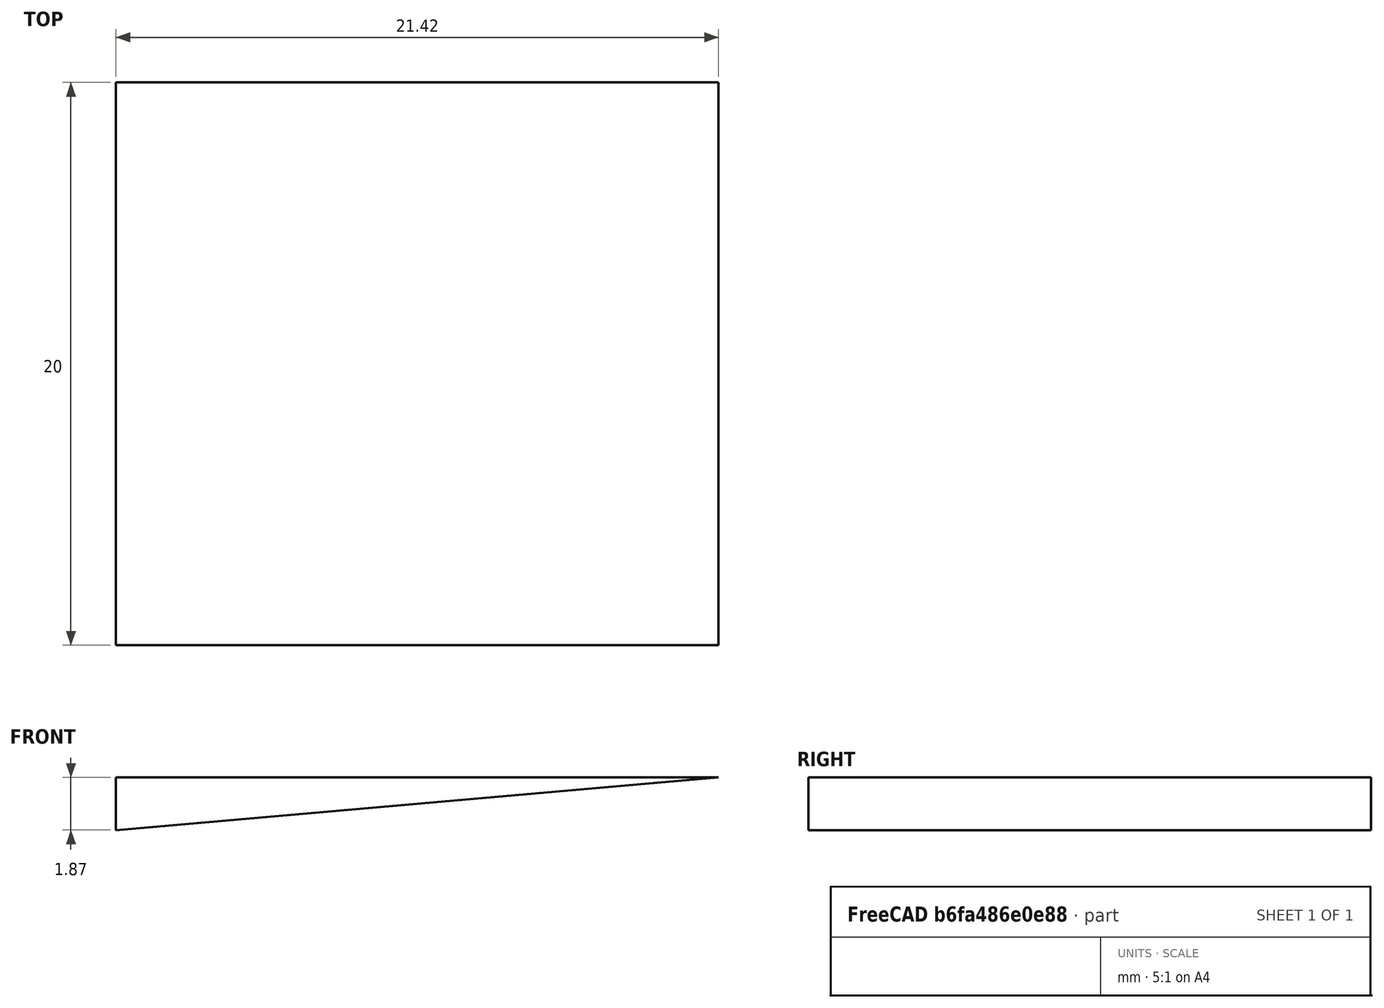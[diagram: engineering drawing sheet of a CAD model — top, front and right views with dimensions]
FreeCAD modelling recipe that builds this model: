
FCSTD DOCUMENT  (FreeCAD 1.0R39109 (Git))
Label: PLASTIC-VSN-DISPLAY-SPACER_3
License: All rights reserved
LicenseURL: https://en.wikipedia.org/wiki/All_rights_reserved
objects: Sketcher::SketchObject×1, PartDesign::Pad×1, PartDesign::Body×1
note: 6 computed .brp shape members not serialized (recipe doc carries the construction recipe); baked Part::Feature solids carry a one-line shape summary decoded from their .brp

FEATURE [Sketcher::SketchObject] Sketch
  ArcFitTolerance = 1e-06
  AttachmentSupport = -> [XZ_Plane]
  FullyConstrained = true
  MakeInternals = false
  MapMode = 5
  Placement = pos=(0,0,0) rot=(1,0,0;1.5708rad)
  sketch-geometry (3):
    g0: LineSegment StartX=10.7091 StartY=0 StartZ=0 EndX=-10.7091 EndY=0 EndZ=0
    g1: LineSegment StartX=-10.7091 StartY=0 StartZ=0 EndX=-10.7091 EndY=-1.87385 EndZ=0
    g2: LineSegment StartX=-10.7091 StartY=-1.87385 StartZ=0 EndX=10.7091 EndY=0 EndZ=0
  constraints (8):
    c: PointOnObject(g0,g-1)
    c: Coincident(g1,g0)
    c: Vertical(g1)
    c: Coincident(g2,g1)
    c: Coincident(g2,g0)
    c: Symmetric(g0,g0,g-1)
    c: Distance(g2) = 21.5
    c: Angle(g0,g2) = 0.0872665
FEATURE [PartDesign::Pad] Pad
  Direction = (0,-1,2e-16)
  Length = 20
  Length2 = 10
  Midplane = true
  Placement = pos=(0,0,0) rot=(1,0,0;1.5708rad)
  Profile = -> Sketch
  ReferenceAxis = -> Sketch [N_Axis]
  Refine = true
  Suppressed = false
  Type = 0
FEATURE [PartDesign::Body] Body
  AllowCompound = false
  Group = -> [Sketch,Pad]
  Origin = -> Origin
  Tip = -> Pad
